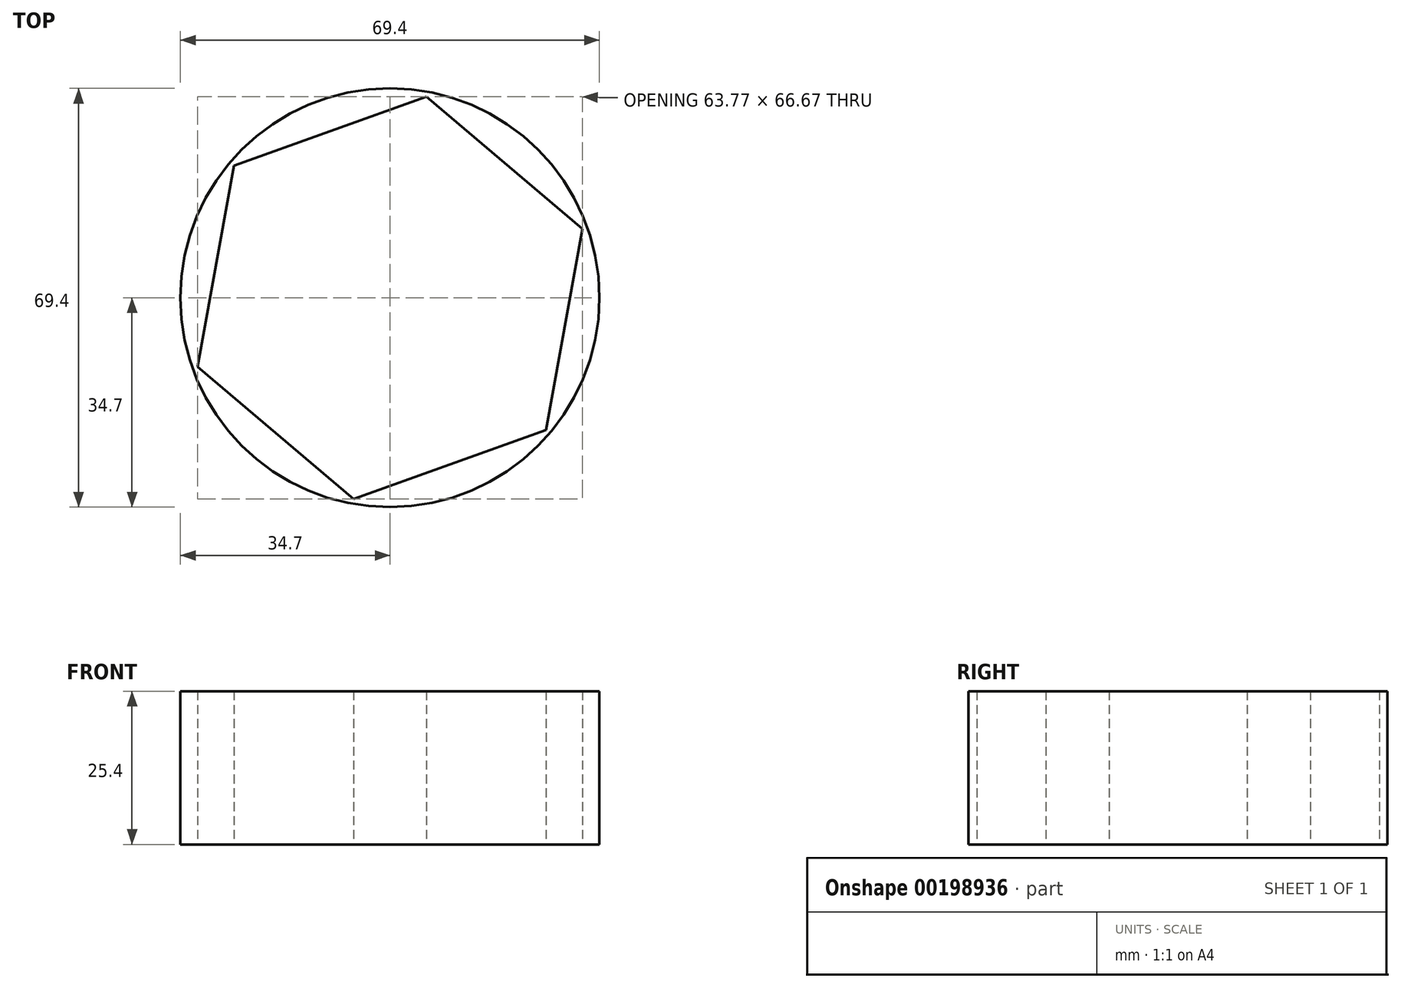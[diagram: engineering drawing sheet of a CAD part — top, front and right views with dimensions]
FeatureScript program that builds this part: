
annotation { "Feature Type Name" : "Feature", "Feature Type Description" : "" }
export const myFeature = defineFeature(function(context is Context, id is Id, definition is map)
    precondition{}
    {
        {
            var Q0;
            Q0=qCreatedBy(makeId("Top.planeOp"),FACE);
            var sketch = newSketch(context, id + "F0", { "sketchPlane" : qUnion([Q0])});
            skCircle(sketch, "E0", {"center": v(0, 0) * mm, "radius": 34.7 * mm});
            skCircle(sketch, "E1.cCircle", {"center": v(0, 0) * mm, "radius": 29.34 * mm, "construction": true});
            skLineSegment(sketch, "E1.0", {"start": v(-25.86, 21.9) * mm, "end": v(6.03, 33.34) * mm});
            skLineSegment(sketch, "E1.1", {"start": v(6.03, 33.34) * mm, "end": v(31.89, 11.45) * mm});
            skLineSegment(sketch, "E1.2", {"start": v(31.89, 11.45) * mm, "end": v(25.86, -21.9) * mm});
            skLineSegment(sketch, "E1.3", {"start": v(25.86, -21.9) * mm, "end": v(-6.03, -33.34) * mm});
            skLineSegment(sketch, "E1.4", {"start": v(-6.03, -33.34) * mm, "end": v(-31.89, -11.45) * mm});
            skLineSegment(sketch, "E1.5", {"start": v(-31.89, -11.45) * mm, "end": v(-25.86, 21.9) * mm});
            skPoint(sketch, "E1.0.midPoint", {"position": v(-9.91, 27.61) * mm});
            skSolve(sketch);
        }
        {
            var Q0;
            Q0=makeQuery(id+"F0.imprint","IMPRINT",FACE,{"disambiguationData":[TD([[makeQuery(id+"F0.imprint","IMPRINT",EDGE,{"derivedFrom":sQuery(id+"F0.wireOp",EDGE,"E0")}),1.0]])]});
            extrude(context, id + "F1", {"entities" : qUnion([Q0]), "depth" : 25.4 * mm});
        }
    });
